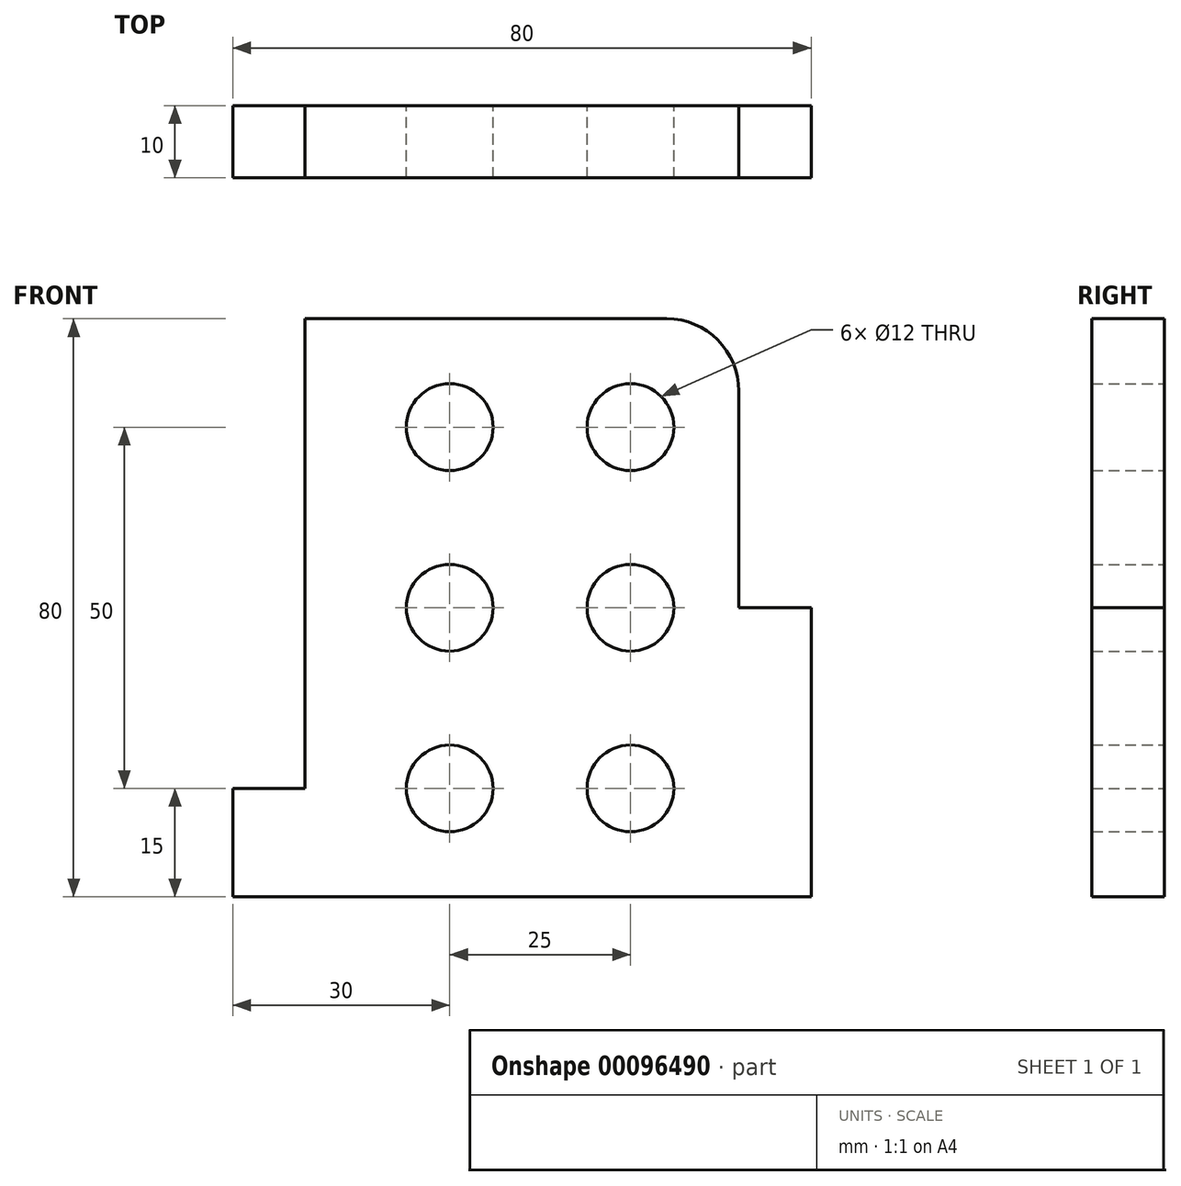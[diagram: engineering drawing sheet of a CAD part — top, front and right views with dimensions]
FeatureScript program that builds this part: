
annotation { "Feature Type Name" : "Feature", "Feature Type Description" : "" }
export const myFeature = defineFeature(function(context is Context, id is Id, definition is map)
    precondition{}
    {
        {
            var Q0;
            Q0=qCreatedBy(makeId("Front.planeOp"),FACE);
            var sketch = newSketch(context, id + "F0", { "sketchPlane" : qUnion([Q0])});
            skLineSegment(sketch, "E0.bottom", {"start": v(0, 0) * mm, "end": v(80, 0) * mm, "construction": true});
            skLineSegment(sketch, "E0.top", {"start": v(0, 80) * mm, "end": v(80, 80) * mm, "construction": true});
            skLineSegment(sketch, "E0.left", {"start": v(0, 0) * mm, "end": v(0, 80) * mm, "construction": true});
            skLineSegment(sketch, "E0.right", {"start": v(80, 0) * mm, "end": v(80, 80) * mm, "construction": true});
            skLineSegment(sketch, "E1", {"start": v(0, 0) * mm, "end": v(0, 15) * mm});
            skLineSegment(sketch, "E2", {"start": v(0, 15) * mm, "end": v(10, 15) * mm});
            skLineSegment(sketch, "E3", {"start": v(10, 15) * mm, "end": v(10, 80) * mm});
            skLineSegment(sketch, "E4", {"start": v(80, 0) * mm, "end": v(80, 40) * mm});
            skLineSegment(sketch, "E5", {"start": v(80, 40) * mm, "end": v(70, 40) * mm});
            skLineSegment(sketch, "E6", {"start": v(70, 40) * mm, "end": v(70, 70) * mm});
            skLineSegment(sketch, "E7", {"start": v(60, 80) * mm, "end": v(10, 80) * mm});
            skPoint(sketch, "E8.visualSharp", {"position": v(70, 80) * mm});
            skArc(sketch, "E8.filletArc", {"start": v(70, 70) * mm, "mid": v(67.07, 77.07) * mm, "end": v(60, 80) * mm});
            skCircle(sketch, "E9.1.0.0", {"center": v(55, 40) * mm, "radius": 6 * mm});
            skCircle(sketch, "E9.2.0.0", {"center": v(55, 15) * mm, "radius": 6 * mm});
            skCircle(sketch, "E10.1.0.0", {"center": v(30, 65) * mm, "radius": 6 * mm});
            skCircle(sketch, "E10.1.0.1", {"center": v(30, 40) * mm, "radius": 6 * mm});
            skCircle(sketch, "E10.1.0.2", {"center": v(30, 15) * mm, "radius": 6 * mm});
            skCircle(sketch, "E11", {"center": v(55, 65) * mm, "radius": 6 * mm});
            skLineSegment(sketch, "E12", {"start": v(0, 0) * mm, "end": v(80, 0) * mm});
            skSolve(sketch);
        }
        {
            var Q0;
            Q0=makeQuery(id+"F0.imprint","IMPRINT",FACE,{"disambiguationData":[TD([[makeQuery(id+"F0.imprint","IMPRINT",EDGE,{"derivedFrom":sQuery(id+"F0.wireOp",EDGE,"E1")}),-1.0]])]});
            extrude(context, id + "F1", {"entities" : qUnion([Q0]), "depth" : 10 * mm});
        }
    });
